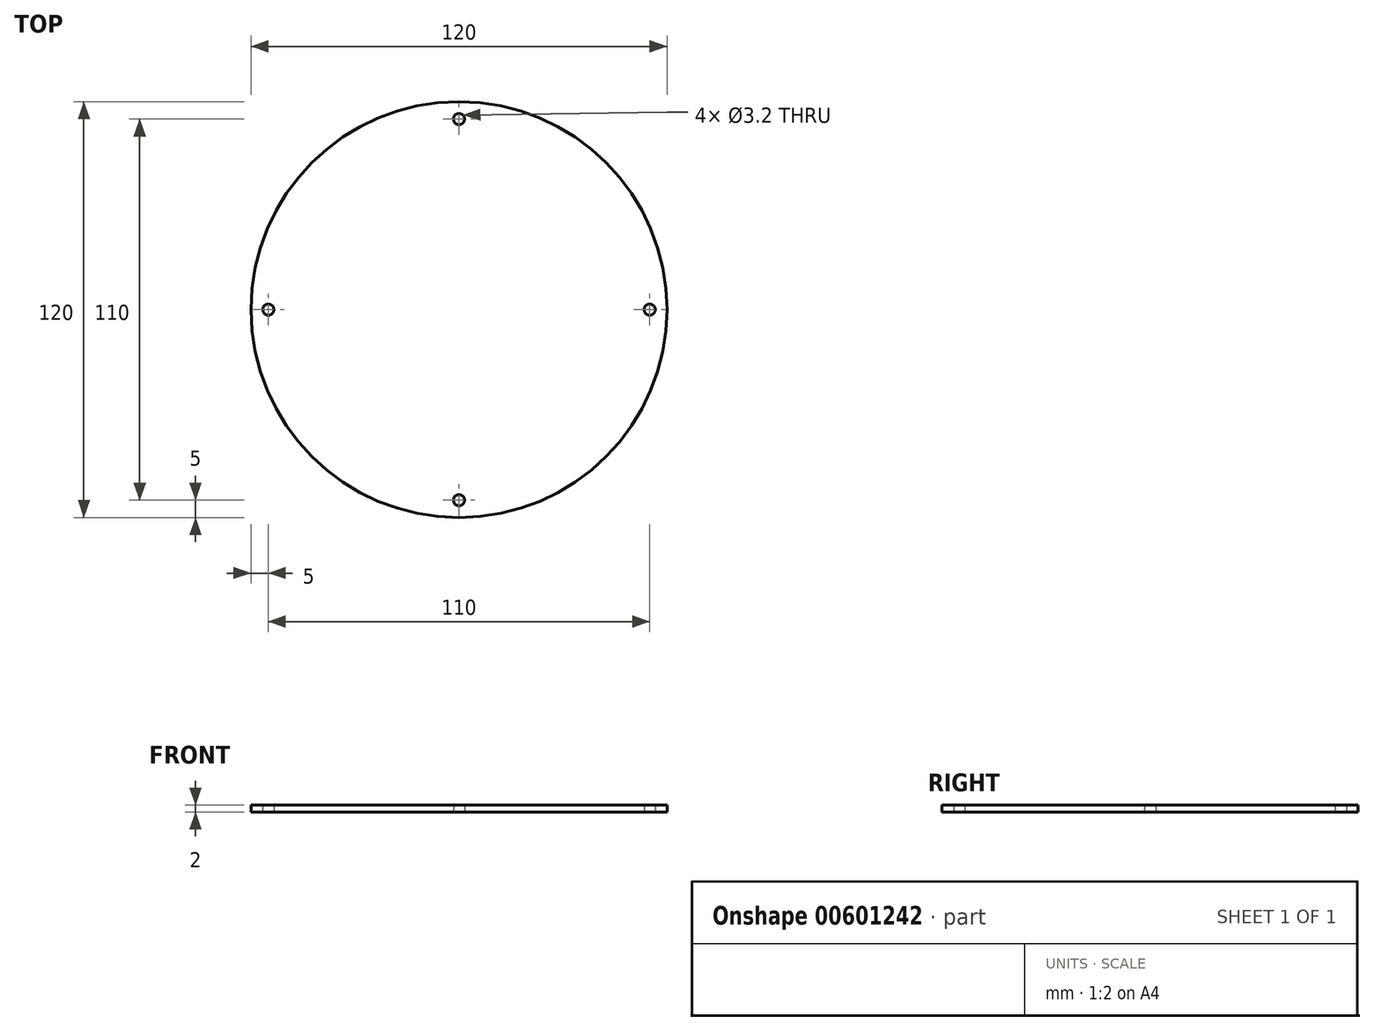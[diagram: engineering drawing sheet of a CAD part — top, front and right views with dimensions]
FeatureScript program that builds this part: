
annotation { "Feature Type Name" : "Feature", "Feature Type Description" : "" }
export const myFeature = defineFeature(function(context is Context, id is Id, definition is map)
    precondition{}
    {
        {
            var Q0;
            Q0=qCreatedBy(makeId("Top.planeOp"),FACE);
            var sketch = newSketch(context, id + "F0", { "sketchPlane" : qUnion([Q0])});
            skCircle(sketch, "E0", {"center": v(0, 0) * mm, "radius": 60 * mm});
            skCircle(sketch, "E1", {"center": v(55, 0) * mm, "radius": 1.6 * mm});
            skCircle(sketch, "E2.1.0", {"center": v(0, 55) * mm, "radius": 1.6 * mm});
            skCircle(sketch, "E2.2.0", {"center": v(-55, 0) * mm, "radius": 1.6 * mm});
            skCircle(sketch, "E2.3.0", {"center": v(0, -55) * mm, "radius": 1.6 * mm});
            skSolve(sketch);
        }
        {
            var Q0;
            Q0=makeQuery(id+"F0.imprint","IMPRINT",FACE,{"disambiguationData":[TD([[makeQuery(id+"F0.imprint","IMPRINT",EDGE,{"derivedFrom":sQuery(id+"F0.wireOp",EDGE,"E0")}),1.0]])]});
            extrude(context, id + "F1", {"entities" : qUnion([Q0]), "depth" : 2 * mm, "offsetDistance" : 25 * mm});
        }
    });
